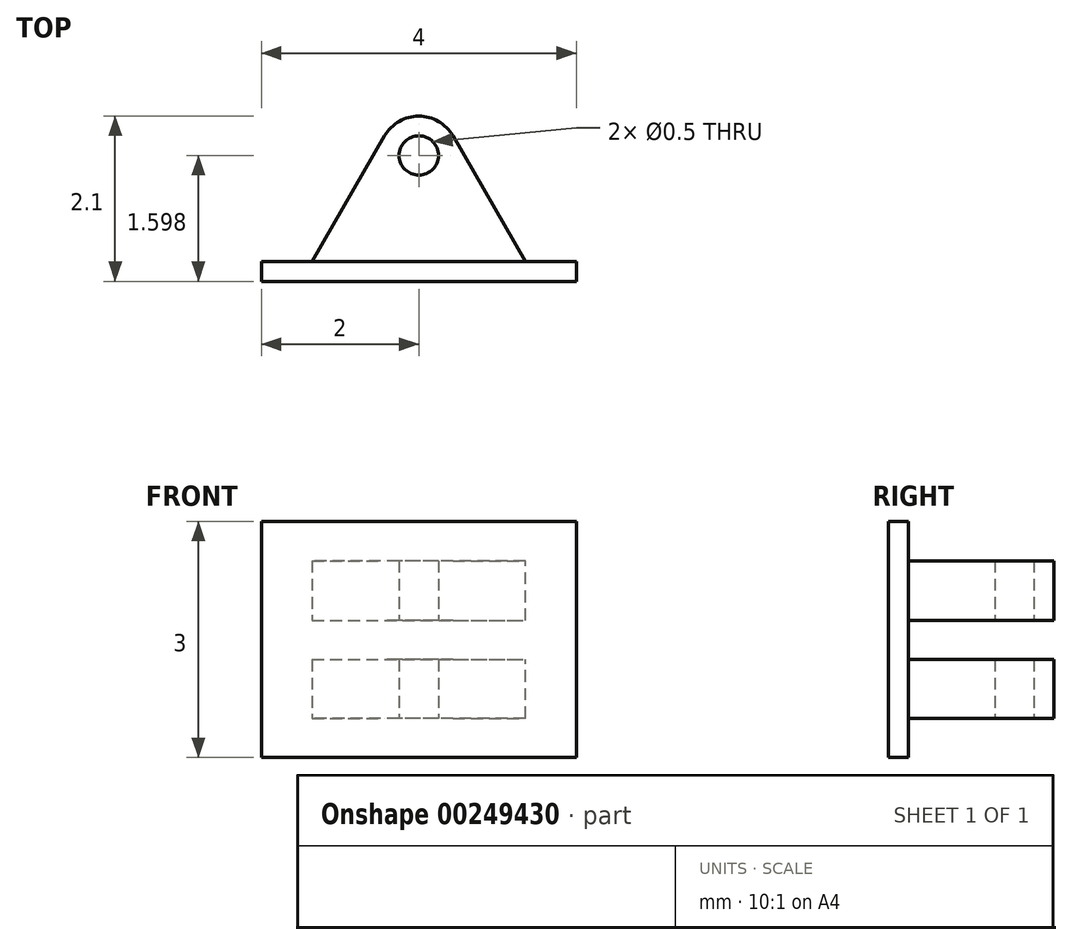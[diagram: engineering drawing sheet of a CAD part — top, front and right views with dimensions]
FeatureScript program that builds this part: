
annotation { "Feature Type Name" : "Feature", "Feature Type Description" : "" }
export const myFeature = defineFeature(function(context is Context, id is Id, definition is map)
    precondition{}
    {
        {
            var Q0;
            Q0=qCreatedBy(makeId("Front.planeOp"),FACE);
            var sketch = newSketch(context, id + "F0", { "sketchPlane" : qUnion([Q0])});
            skLineSegment(sketch, "E0.bottom", {"start": v(2, 1.5) * mm, "end": v(-2, 1.5) * mm});
            skLineSegment(sketch, "E0.top", {"start": v(2, -1.5) * mm, "end": v(-2, -1.5) * mm});
            skLineSegment(sketch, "E0.left", {"start": v(2, 1.5) * mm, "end": v(2, -1.5) * mm});
            skLineSegment(sketch, "E0.right", {"start": v(-2, 1.5) * mm, "end": v(-2, -1.5) * mm});
            skPoint(sketch, "E0.middle", {"position": v(0, 0) * mm});
            skSolve(sketch);
        }
        {
            var Q0;
            Q0=makeQuery(id+"F0.imprint","IMPRINT",FACE,{"disambiguationData":[TD([[makeQuery(id+"F0.imprint","IMPRINT",EDGE,{"derivedFrom":sQuery(id+"F0.wireOp",EDGE,"E0.bottom")}),1.0]])]});
            extrude(context, id + "F1", {"entities" : qUnion([Q0]), "depth" : 0.25 * mm});
        }
        {
            var Q0;
            Q0=qCreatedBy(makeId("Top.planeOp"),FACE);
            var sketch = newSketch(context, id + "F2", { "sketchPlane" : qUnion([Q0])});
            skLineSegment(sketch, "E1.0", {"start": v(2, -0.25) * mm, "end": v(-2, -0.25) * mm});
            skLineSegment(sketch, "E2", {"start": v(-1.5, -0.25) * mm, "end": v(-0.43, 1.6) * mm});
            skLineSegment(sketch, "E3", {"start": v(0.43, 1.6) * mm, "end": v(1.5, -0.25) * mm});
            skLineSegment(sketch, "E4", {"start": v(1.5, -0.25) * mm, "end": v(-1.5, -0.25) * mm});
            skArc(sketch, "E5", {"start": v(0.43, 1.6) * mm, "mid": v(0, 1.85) * mm, "end": v(-0.43, 1.6) * mm});
            skPoint(sketch, "E6.orphan", {"position": v(0, 2.35) * mm});
            skCircle(sketch, "E7", {"center": v(0, 1.35) * mm, "radius": 0.25 * mm});
            skSolve(sketch);
        }
        {
            var Q0;
            Q0 = qSketchRegion(id + "F2", true);
            extrude(context, id + "F3", {"entities" : qUnion([Q0]), "operationType" : NewBodyOperationType.ADD, "endBound" : BoundingType.SYMMETRIC, "depth" : 2 * mm});
        }
        {
            var Q0;
            Q0=qCreatedBy(makeId("Right.planeOp"),FACE);
            var sketch = newSketch(context, id + "F4", { "sketchPlane" : qUnion([Q0])});
            skLineSegment(sketch, "E8.bottom", {"start": v(2.06, 0.24) * mm, "end": v(0, 0.24) * mm});
            skLineSegment(sketch, "E8.top", {"start": v(2.06, -0.26) * mm, "end": v(0, -0.26) * mm});
            skLineSegment(sketch, "E8.left", {"start": v(2.06, 0.24) * mm, "end": v(2.06, -0.26) * mm});
            skLineSegment(sketch, "E8.right", {"start": v(0, 0.24) * mm, "end": v(0, -0.26) * mm});
            skLineSegment(sketch, "E9.bottom", {"start": v(2.06, 0.24) * mm, "end": v(2.06, 0.24) * mm});
            skLineSegment(sketch, "E9.top", {"start": v(2.06, -0.26) * mm, "end": v(2.06, -0.26) * mm});
            skSolve(sketch);
        }
        {
            var Q0;
            Q0 = qSketchRegion(id + "F4", true);
            extrude(context, id + "F5", {"entities" : qUnion([Q0]), "operationType" : NewBodyOperationType.REMOVE, "endBound" : BoundingType.SYMMETRIC, "oppositeDirection" : true, "depth" : 25 * mm});
        }
    });
